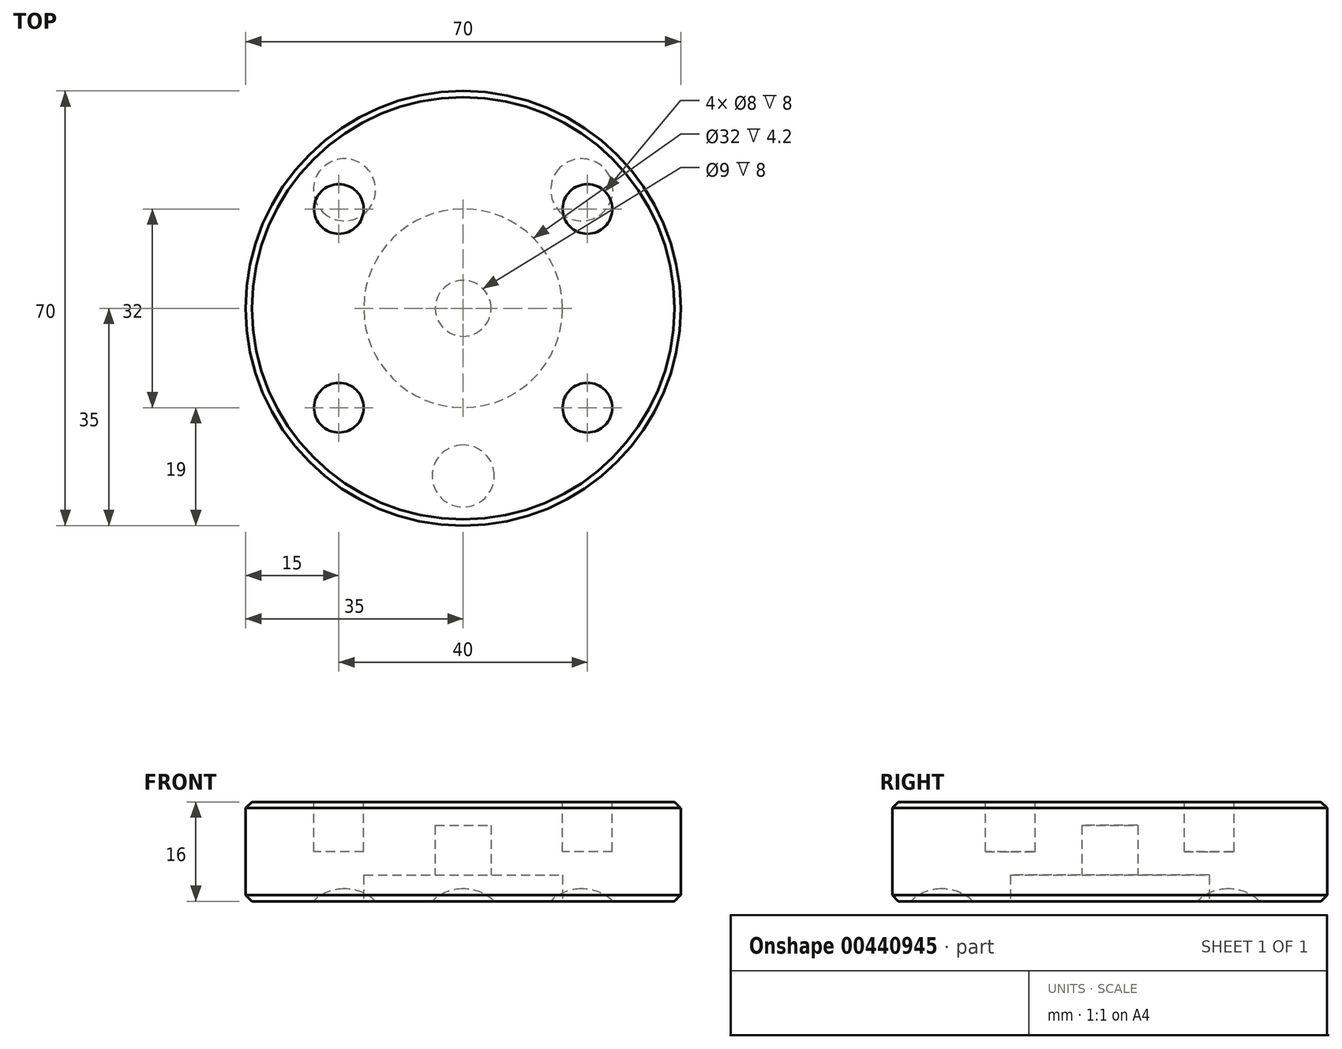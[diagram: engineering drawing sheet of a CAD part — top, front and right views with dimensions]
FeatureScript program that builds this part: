
annotation { "Feature Type Name" : "Feature", "Feature Type Description" : "" }
export const myFeature = defineFeature(function(context is Context, id is Id, definition is map)
    precondition{}
    {
        {
            var Q0;
            Q0=qCreatedBy(makeId("Top.planeOp"),FACE);
            var sketch = newSketch(context, id + "F0", { "sketchPlane" : qUnion([Q0])});
            skCircle(sketch, "E0", {"center": v(0, 0) * mm, "radius": 35 * mm});
            skSolve(sketch);
        }
        {
            var Q0;
            Q0=qCreatedBy(makeId("Front.planeOp"),FACE);
            var sketch = newSketch(context, id + "F1", { "sketchPlane" : qUnion([Q0])});
            skLineSegment(sketch, "E1", {"start": v(0, 0) * mm, "end": v(0, 40) * mm, "construction": true});
            skSolve(sketch);
        }
        {
            var Q0;
            Q0=makeQuery(id+"F0.imprint","IMPRINT",FACE,{"disambiguationData":[TD([[makeQuery(id+"F0.imprint","IMPRINT",EDGE,{"derivedFrom":sQuery(id+"F0.wireOp",EDGE,"E0")}),1.0]])]});
            extrude(context, id + "F2", {"entities" : qUnion([Q0]), "depth" : 16 * mm});
        }
        {
            var Q0;
            Q0=makeQuery(id+"F2.opExtrude","CAP_FACE",FACE,{"disambiguationData":[OSD([sQuery(id+"F0.wireOp",EDGE,"E0")])],"isStart":false});
            var sketch = newSketch(context, id + "F3", { "sketchPlane" : qUnion([Q0])});
            skPoint(sketch, "E2", {"position": v(0, 0) * mm});
            skLineSegment(sketch, "E3.bottom", {"start": v(20, 16) * mm, "end": v(-20, 16) * mm, "construction": true});
            skLineSegment(sketch, "E3.top", {"start": v(20, -16) * mm, "end": v(-20, -16) * mm, "construction": true});
            skLineSegment(sketch, "E3.left", {"start": v(20, 16) * mm, "end": v(20, -16) * mm, "construction": true});
            skLineSegment(sketch, "E3.right", {"start": v(-20, 16) * mm, "end": v(-20, -16) * mm, "construction": true});
            skCircle(sketch, "E4", {"center": v(20, 16) * mm, "radius": 4 * mm});
            skCircle(sketch, "E5", {"center": v(20, -16) * mm, "radius": 4 * mm});
            skCircle(sketch, "E6", {"center": v(-20, -16) * mm, "radius": 4 * mm});
            skCircle(sketch, "E7", {"center": v(-20, 16) * mm, "radius": 4 * mm});
            skSolve(sketch);
        }
        {
            var Q0;
            Q0=makeQuery(id+"F2.opExtrude","CAP_FACE",FACE,{"disambiguationData":[OSD([sQuery(id+"F0.wireOp",EDGE,"E0")])],"isStart":true});
            var sketch = newSketch(context, id + "F4", { "sketchPlane" : qUnion([Q0])});
            skPoint(sketch, "E8", {"position": v(27, 0) * mm});
            skPoint(sketch, "E9.1.0", {"position": v(19.1, 19.1) * mm});
            skPoint(sketch, "E9.2.0", {"position": v(0, 27) * mm});
            skPoint(sketch, "E9.3.0", {"position": v(-19.1, 19.1) * mm});
            skPoint(sketch, "E9.4.0", {"position": v(-27, 0) * mm});
            skPoint(sketch, "E9.5.0", {"position": v(-19.1, -19.1) * mm});
            skPoint(sketch, "E9.6.0", {"position": v(0, -27) * mm});
            skPoint(sketch, "E9.7.0", {"position": v(19.1, -19.1) * mm});
            skCircle(sketch, "E10", {"center": v(0, 0) * mm, "radius": 16 * mm});
            skSolve(sketch);
        }
        {
            var Q0;
            Q0=makeQuery(id+"F4.imprint","IMPRINT",FACE,{"disambiguationData":[TD([[makeQuery(id+"F4.imprint","IMPRINT",EDGE,{"derivedFrom":sQuery(id+"F4.wireOp",EDGE,"E10")}),1.0]])]});
            extrude(context, id + "F5", {"entities" : qUnion([Q0]), "operationType" : NewBodyOperationType.REMOVE, "oppositeDirection" : true, "depth" : 4.2 * mm});
        }
        {
            var Q0;
            Q0=makeQuery(id+"F5.boolean.opBoolean","COPY",FACE,{"derivedFrom":makeQuery(id+"F5.opExtrude","CAP_FACE",FACE,{"disambiguationData":[OSD([sQuery(id+"F4.wireOp",EDGE,"E10")])],"isStart":false})});
            var sketch = newSketch(context, id + "F6", { "sketchPlane" : qUnion([Q0])});
            skCircle(sketch, "E11", {"center": v(0, 0) * mm, "radius": 4.5 * mm});
            skSolve(sketch);
        }
        {
            var Q0;
            Q0=makeQuery(id+"F6.imprint","IMPRINT",FACE,{"disambiguationData":[TD([[makeQuery(id+"F6.imprint","IMPRINT",EDGE,{"derivedFrom":sQuery(id+"F6.wireOp",EDGE,"E11")}),1.0]])]});
            extrude(context, id + "F7", {"entities" : qUnion([Q0]), "operationType" : NewBodyOperationType.REMOVE, "oppositeDirection" : true, "depth" : 8 * mm});
        }
        {
            var Q0;
            Q0=qCreatedBy(makeId("Right.planeOp"),FACE);
            var sketch = newSketch(context, id + "F8", { "sketchPlane" : qUnion([Q0])});
            skLineSegment(sketch, "E12", {"start": v(-32, 0) * mm, "end": v(-22, 0) * mm});
            skArc(sketch, "E13", {"start": v(-22, 0) * mm, "mid": v(-27, 2) * mm, "end": v(-32, 0) * mm});
            skLineSegment(sketch, "E14", {"start": v(-27, 0) * mm, "end": v(-27, 2) * mm});
            skSolve(sketch);
        }
        {
            var Q0;
            {var subQ3=sQuery(id+"F8.wireOp",EDGE,"E14");Q0=makeQuery(id+"F8.imprint","IMPRINT",FACE,{"disambiguationData":[TD([[makeQuery(id+"F8.imprint","IMPRINT",EDGE,{"derivedFrom":subQ3}),-1.0]])]});}
            var Q1;
            Q1=sQuery(id+"F8.wireOp",EDGE,"E14");
            revolve(context, id + "F9", {"entities" : qUnion([Q0]), "axis" : qUnion([Q1]), "revolveType" : RevolveType.FULL, "oppositeDirection" : true});
        }
        {
            var Q0;
            Q0=makeQuery(id+"F3.imprint","IMPRINT",FACE,{"disambiguationData":[TD([[makeQuery(id+"F3.imprint","IMPRINT",EDGE,{"derivedFrom":sQuery(id+"F3.wireOp",EDGE,"E7")}),1.0]])]});
            var Q1;
            Q1=makeQuery(id+"F3.imprint","IMPRINT",FACE,{"disambiguationData":[TD([[makeQuery(id+"F3.imprint","IMPRINT",EDGE,{"derivedFrom":sQuery(id+"F3.wireOp",EDGE,"E6")}),1.0]])]});
            var Q2;
            Q2=makeQuery(id+"F3.imprint","IMPRINT",FACE,{"disambiguationData":[TD([[makeQuery(id+"F3.imprint","IMPRINT",EDGE,{"derivedFrom":sQuery(id+"F3.wireOp",EDGE,"E4")}),1.0]])]});
            var Q3;
            Q3=makeQuery(id+"F3.imprint","IMPRINT",FACE,{"disambiguationData":[TD([[makeQuery(id+"F3.imprint","IMPRINT",EDGE,{"derivedFrom":sQuery(id+"F3.wireOp",EDGE,"E5")}),1.0]])]});
            extrude(context, id + "F10", {"entities" : qUnion([Q0, Q1, Q2, Q3]), "operationType" : NewBodyOperationType.REMOVE, "oppositeDirection" : true, "depth" : 8 * mm});
        }
        {
            var Q0;
            Q0=makeQuery(id+"F9.opRevolve","SWEPT_BODY",BODY,{"disambiguationData":[OSD([sQuery(id+"F8.wireOp",EDGE,"E12"),sQuery(id+"F8.wireOp",EDGE,"E13"),sQuery(id+"F8.wireOp",EDGE,"E14")])]});
            var Q1;
            Q1=sQuery(id+"F1.wireOp",EDGE,"E1");
            circularPattern(context, id + "F11", {"operationType" : NewBodyOperationType.REMOVE, "entities" : qUnion([Q0]), "axis" : qUnion([Q1]), "angle" : 135 * degree, "instanceCount" : 2, "isCentered" : true});
        }
        {
            var Q0;
            Q0=makeQuery(id+"F5.boolean.opBoolean","COPY",EDGE,{"derivedFrom":makeQuery(id+"F5.opExtrude","CAP_EDGE",EDGE,{"disambiguationData":[OSD([sQuery(id+"F4.wireOp",EDGE,"E10")])],"isStart":true})});
            var Q1;
            Q1=makeQuery(id+"F2.opExtrude","CAP_EDGE",EDGE,{"disambiguationData":[OSD([sQuery(id+"F0.wireOp",EDGE,"E0")])],"isStart":true});
            var Q2;
            Q2=makeQuery(id+"F2.opExtrude","CAP_EDGE",EDGE,{"disambiguationData":[OSD([sQuery(id+"F0.wireOp",EDGE,"E0")])],"isStart":false});
            var Q3;
            Q3=makeQuery(id+"F7.boolean.opBoolean","COPY",EDGE,{"derivedFrom":makeQuery(id+"F7.opExtrude","CAP_EDGE",EDGE,{"disambiguationData":[OSD([sQuery(id+"F6.wireOp",EDGE,"E11")])],"isStart":true})});
            chamfer(context, id + "F12", {"entities" : qUnion([Q0, Q1, Q2, Q3]), "width" : 1 * mm, "tangentPropagation" : true});
        }
    });
